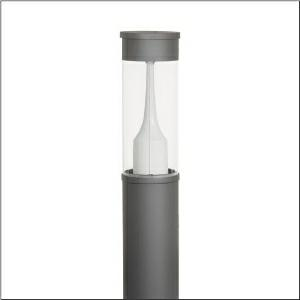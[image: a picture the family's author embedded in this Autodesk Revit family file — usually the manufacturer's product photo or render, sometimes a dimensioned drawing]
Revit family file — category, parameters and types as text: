
# Revit family: city-light_400_iq___st1_2a_5xa5305kf14h_7e7c
name_source: partatom
category: Lighting Fixtures
units: mm (PartAtom-declared; Revit-internal decimal feet)

## family parameters
Cut with Voids When Loaded = No
Host = Face
Light Source = No
Part Type = Normal
Room Calculation Point = No
Round Connector Dimension = Use Diameter
Shared = No

## types (1)
- --- (1 x LED, 1540 lm, 10 W, 4000K)
    Apparent Load = 10 VA
    CIE Flux Codes = 22 61 93 96 100
    Color Rendering = 70
    Color Temperature = 4000K
    Default Elevation = 1800 mm
    Description = City-Light 400 iQ, light pillar, Module 540 iQ-SR, primary light control with 3 zone facetted reflector, of plastic, silver coated, highly specular, structured, primary optical cover: cover, of PMMA, transparent, partly coated, light distribution: ST1.2a, primary light characteristic: asymmetric, LED, High Power LED, rated luminous flux: 1.540lm, luminous efficacy: 154lm/W, light colour: 740, colour temperature: 4000K, control gear: ECG iQ, control: presetting dimming logarithmic, Street-Remote, Auto-Match, Temp-Guard, Lumen-Switch, Night-Set, Smart-Wire, Light-Fading, Desk-Remote (wireless, voltage-free reading and setting of iQ features in the workshop via application-optimized NFC function/RFID function), optimised constant luminous flux control (CLO 2.0), with terminal, 6-pole, max. 2.5mm², mains connection: 220..240V, AC, 50/60Hz, start of lifetime: 10W, end of lifetime: 10W, reduction: 5W, luminaire housing, cylindrical, of extruded aluminium section, coated, Siteco® metallic grey (DB 702S), length: 4.694mm, diameter: 200mm, Module 540 iQ-SR, traffic white (RAL 9016), equipment: standard, protection rating (complete): IP65, insulation class (complete): insulation class II (safety insulation), certification: CE, ENEC, VDE, packaging unit: 1 piece

Light Distribution: ST1.2a
    Height = 500 mm
    Lamp = 1 x LED
    Lamp Light Flux = 1540 lm
    Lamp Power = 10 W
    Lamp count = 1
    Length = 200 mm  [stored 0.656168 ft]
    Luminous efficacy = 154 lm/W
    Manufacturer = Siteco
    ModVariant = No
    Model = 5XA5305KF14H
    Mounting Place = Floor
    Mounting Type = Freestanding
    Number of Poles = 1
    OnlyDefault = Yes
    Power Factor = 1
    Product Name = City-Light 400 iQ | ST1.2a
    Product group = light pillar | freestanding
    ProductGroupID = 1301
    Protection Class = Protection class II
    Protection Degree = IP 65
    RLX_Detail_Level = 1
    RlxData = <blob elided: 87429 chars, md5=d9d0921f>
    Socket = socket
    Standby Power = 0 W
    System Light Flux = 1540 lm
    System Power = 10 W
    Type Comments = factory setting: luminous flux: 100 % | dim-lin: 254 | 401 mA
    Type Image = l_1006914.jpg
    URL = http://relux.com
    VarID = @adj_070319
    Voltage = 0 V
    Weight = 0.00 kg
    Width = 0 mm  [stored 0 ft]

note: [stored X ft] marks values corroborated as IEEE doubles in the binary element streams (Revit-internal decimal feet)

## geometry (parser evidence)
native form markers: Blend x4, Sweep x11
no freeform markers — native parametric forms only
